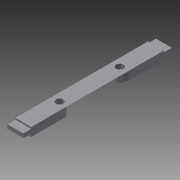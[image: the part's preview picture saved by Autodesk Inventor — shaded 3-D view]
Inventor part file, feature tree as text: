
AUTODESK INVENTOR PART (.ipt)
format: ipt  version: 2015 (Build 190159000, 159)  size: 295,936 bytes
history: native  units: in
note: dims shown in document units (in); Inventor stores cm internally (conversion verified against a paired STEP export)
features: extrude x8, sketch x7, projected_geometry x7, fillet x4, reference x2, chamfer x1
ambient origin geometry x8: Origin, YZ Plane, XZ Plane, XY Plane, X Axis, Y Axis, Z Axis, Center Point
bodies: Solid1 (feature_tree)
feature tree (29):
  extrude  "Extrusion1"  Depth=0.25in
  extrude  "Extrusion2"  Depth=0.25in
  extrude  "Extrusion3"  Depth=4.8in TaperAngle=0.0deg
  extrude  "Extrusion4"  Depth=0.1in TaperAngle=0.0deg
  chamfer  "Chamfer1"  Distance=0.0625in
  fillet  "Fillet1"  Radius=0.375in
  extrude  "Extrusion6"  Depth=0.3in TaperAngle=0.0deg
  extrude  "Extrusion5"  Depth=0.125in
  extrude  "Extrusion7"  Depth=0.125in TaperAngle=0.0deg
  fillet  "Fillet2"  Radius=0.1875in
  fillet  "Fillet3"  Radius=0.0425in
  extrude  "Extrusion8"  Depth=0.125in
  fillet  "Fillet4"  [1 undecoded]
  sketch  "Sketch1"  dims[d0=1.0in d1=0.25in]
  sketch  "Sketch2"  dims[d2=9.3625in d3=0.0in d6=0.25in]
  projected_geometry  "Projected Loop1"
  sketch  "Sketch3"  dims[d7=0.25in d8=4.8in d9=0.0in]
  reference  "Reference1"
  reference  "Reference2"
  projected_geometry  "Projected Loop2"
  sketch  "Sketch5"  dims[d10=3.8in d11=0.1in d12=0.0in d13=0.0625in d14=0.0in]
  projected_geometry  "Projected Loop4"
  sketch  "Sketch6"  dims[d15=0.25in d16=0.9375in d17=45.0deg d18=0.375in]
  projected_geometry  "Projected Loop5"
  projected_geometry  "Projected Loop6"
  sketch  "Sketch9"  dims[d19=0.4375in d20=0.3in d21=0.0in]
  projected_geometry  "Projected Loop7"
  projected_geometry  "Projected Loop8"
  sketch  "Sketch10"  dims[d22=0.6562in d23=0.0in d24=0.624in d25=0.1875in d26=0.0in d27=0.1875in d28=0.0425in d29=0.25in d30=0.0in d31=0.0in d32=0.25in d33=0.125in]
note: 1 required parameter value undecoded (feature->parameter linkage not recoverable at this tier; creation-order binding heuristic only, values carry confidence <= 0.55)
